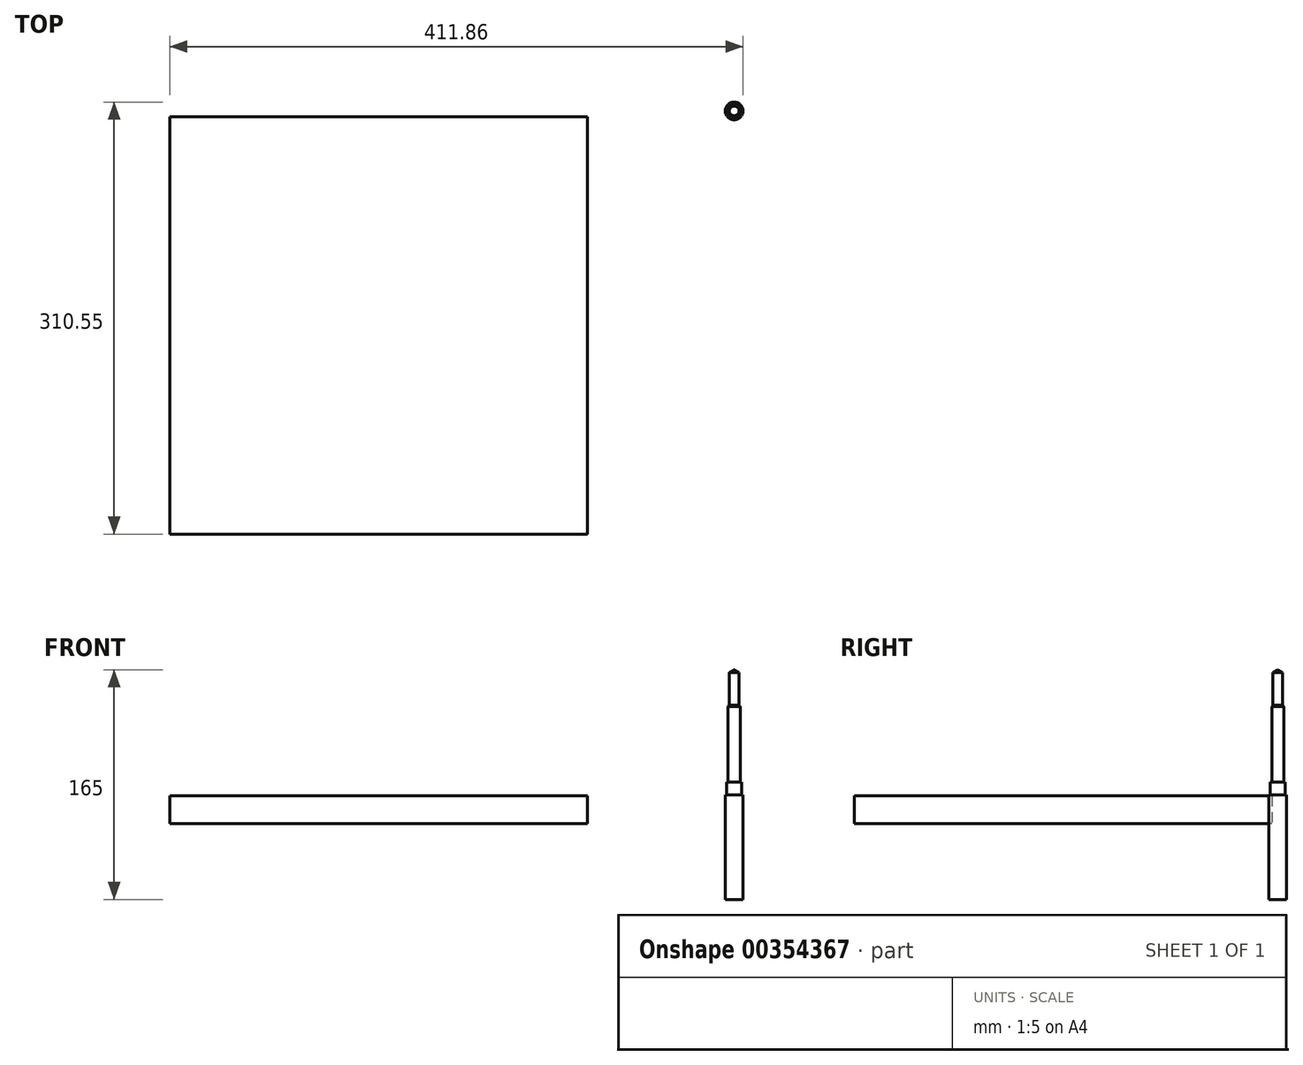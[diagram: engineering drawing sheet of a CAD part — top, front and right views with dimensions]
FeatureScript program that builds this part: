
annotation { "Feature Type Name" : "Feature", "Feature Type Description" : "" }
export const myFeature = defineFeature(function(context is Context, id is Id, definition is map)
    precondition{}
    {
        {
            var Q0;
            Q0=qCreatedBy(makeId("Front.planeOp"),FACE);
            var sketch = newSketch(context, id + "F0", { "sketchPlane" : qUnion([Q0])});
            skLineSegment(sketch, "E0", {"start": v(0, 110.6) * mm, "end": v(0, -41.4) * mm});
            skLineSegment(sketch, "E1", {"start": v(0, 110.6) * mm, "end": v(3.5, 108.6) * mm});
            skLineSegment(sketch, "E2", {"start": v(3.5, 108.6) * mm, "end": v(3.5, 85.1) * mm});
            skLineSegment(sketch, "E3", {"start": v(4.3, 84.1) * mm, "end": v(4.3, 29.8) * mm});
            skLineSegment(sketch, "E4", {"start": v(5.5, 29.8) * mm, "end": v(5.5, 20.6) * mm});
            skLineSegment(sketch, "E5", {"start": v(6.35, 20.6) * mm, "end": v(6.35, -41.4) * mm});
            skLineSegment(sketch, "E6", {"start": v(3.5, 85.1) * mm, "end": v(4.3, 84.1) * mm});
            skLineSegment(sketch, "E7", {"start": v(4.3, 29.8) * mm, "end": v(5.5, 29.8) * mm});
            skLineSegment(sketch, "E8", {"start": v(5.5, 20.6) * mm, "end": v(6.35, 20.6) * mm});
            skLineSegment(sketch, "E9", {"start": v(0, -41.4) * mm, "end": v(6.35, -41.4) * mm});
            skSolve(sketch);
        }
        {
            var Q0;
            Q0=makeQuery(id+"F0.imprint","IMPRINT",FACE,{"disambiguationData":[TD([[makeQuery(id+"F0.imprint","IMPRINT",EDGE,{"derivedFrom":sQuery(id+"F0.wireOp",EDGE,"E0")}),1.0]])]});
            var Q1;
            Q1=sQuery(id+"F0.wireOp",EDGE,"E0");
            revolve(context, id + "F1", {"entities" : qUnion([Q0]), "axis" : qUnion([Q1]), "revolveType" : RevolveType.FULL});
        }
        {
            var Q0;
            Q0=qCreatedBy(makeId("Top.planeOp"),FACE);
            var sketch = newSketch(context, id + "F2", { "sketchPlane" : qUnion([Q0])});
            skLineSegment(sketch, "E10.bottom", {"start": v(-405.51, -4.2) * mm, "end": v(-105.51, -4.2) * mm});
            skLineSegment(sketch, "E10.top", {"start": v(-405.51, -304.2) * mm, "end": v(-105.51, -304.2) * mm});
            skLineSegment(sketch, "E10.left", {"start": v(-405.51, -4.2) * mm, "end": v(-405.51, -304.2) * mm});
            skLineSegment(sketch, "E10.right", {"start": v(-105.51, -4.2) * mm, "end": v(-105.51, -304.2) * mm});
            skSolve(sketch);
        }
        {
            var Q0;
            Q0=makeQuery(id+"F2.imprint","IMPRINT",FACE,{"disambiguationData":[TD([[makeQuery(id+"F2.imprint","IMPRINT",EDGE,{"derivedFrom":sQuery(id+"F2.wireOp",EDGE,"E10.bottom")}),-1.0]])]});
            extrude(context, id + "F3", {"entities" : qUnion([Q0]), "depth" : 20 * mm});
        }
        {
            var Q0;
            Q0=makeQuery(id+"F1.opRevolve","SWEPT_FACE",FACE,{"disambiguationData":[OSD([sQuery(id+"F0.wireOp",EDGE,"mtD2Yns0-krQL-wVmn-sxQQ-XKqHqdHqEuP6")])]});
            var Q1;
            Q1=makeQuery(id+"F1.opRevolve","SWEPT_FACE",FACE,{"disambiguationData":[OSD([sQuery(id+"F0.wireOp",EDGE,"E9")])]});
            extrude(context, id + "F4", {"entities" : qUnion([Q0, Q1]), "operationType" : NewBodyOperationType.ADD, "depth" : 13 * mm});
        }
    });
